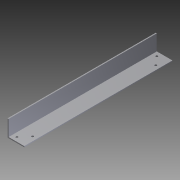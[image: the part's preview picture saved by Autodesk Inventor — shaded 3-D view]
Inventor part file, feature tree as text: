
AUTODESK INVENTOR PART (.ipt)
format: ipt  version: 2012 (Build 160160000, 160)  size: 91,136 bytes
history: native  units: in
note: dims shown in document units (in); Inventor stores cm internally (conversion verified against a paired STEP export)
features: extrude x2, sketch x2
ambient origin geometry x8: Origin, YZ Plane, XZ Plane, XY Plane, X Axis, Y Axis, Z Axis, Center Point
bodies: Solid1 (feature_tree)
feature tree (4):
  extrude  "Extrusion1"  Depth=0.0625in
  extrude  "Extrusion2"  Depth=1.0in
  sketch  "Sketch1"  dims[d0=0.0625in d1=0.0625in]
  sketch  "Sketch2"  dims[d2=1.0in d3=1.0in d4=8.875in d5=0.0in d6=0.125in d7=0.25in d8=0.3125in d9=0.75in d10=0.25in d11=8.875in d12=0.0in]
